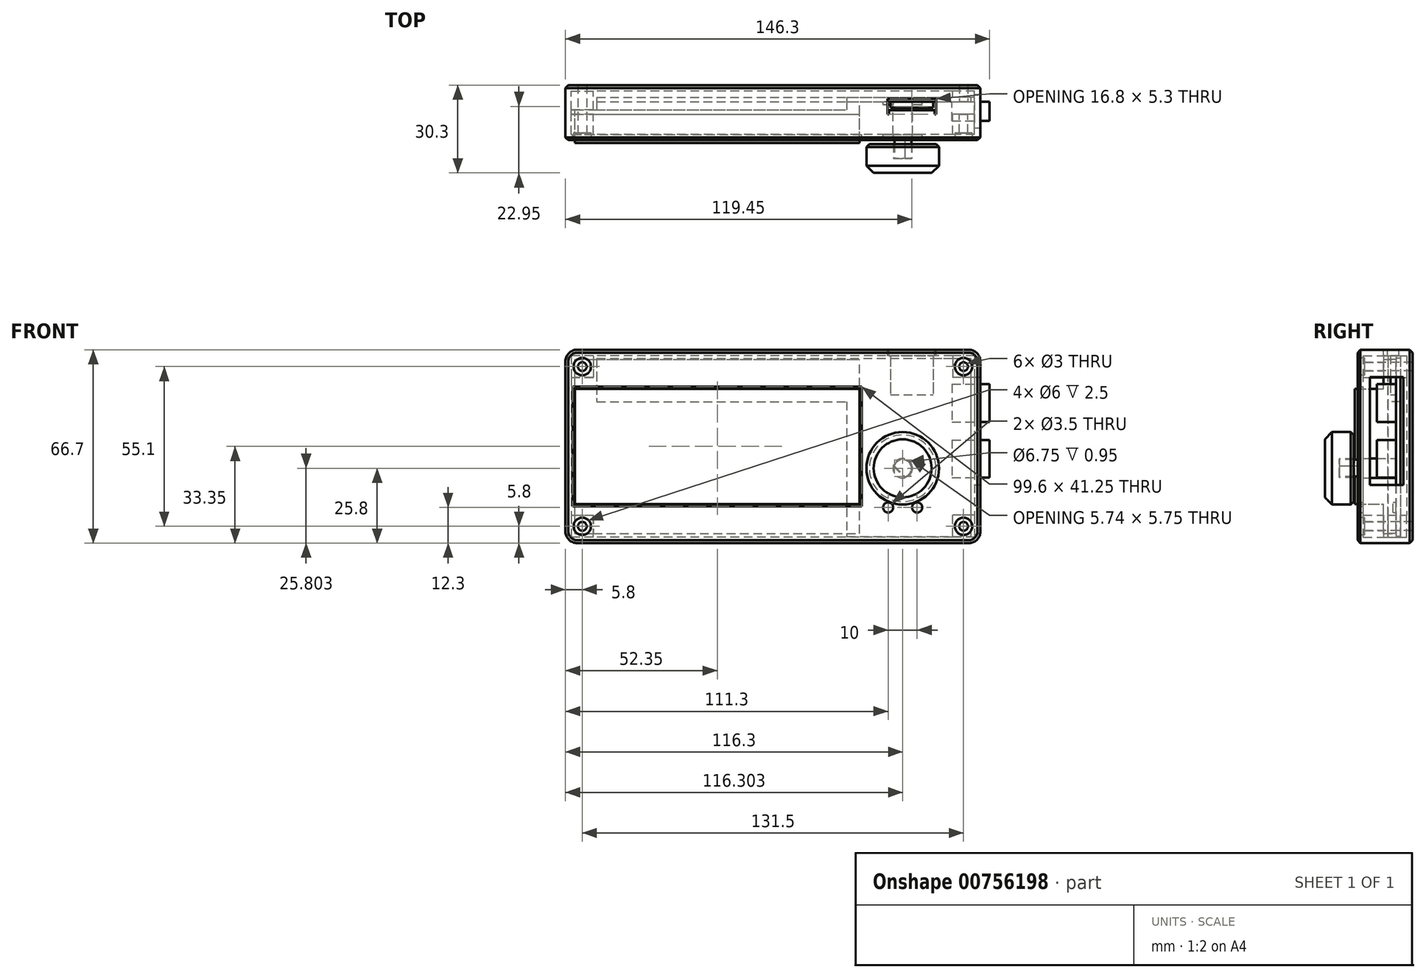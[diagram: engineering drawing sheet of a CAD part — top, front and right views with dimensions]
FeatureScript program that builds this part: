
annotation { "Feature Type Name" : "Feature", "Feature Type Description" : "" }
export const myFeature = defineFeature(function(context is Context, id is Id, definition is map)
    precondition{}
    {
        {
            var Q0;
            Q0=qCreatedBy(makeId("Front.planeOp"),FACE);
            var sketch = newSketch(context, id + "F0", { "sketchPlane" : qUnion([Q0])});
            skLineSegment(sketch, "E0.bottom", {"start": v(0, 0) * mm, "end": v(98.1, 0) * mm});
            skLineSegment(sketch, "E0.top", {"start": v(0, 60.1) * mm, "end": v(98.1, 60.1) * mm});
            skLineSegment(sketch, "E0.left", {"start": v(0, 0) * mm, "end": v(0, 60.1) * mm});
            skLineSegment(sketch, "E0.right", {"start": v(98.1, 0) * mm, "end": v(98.1, 60.1) * mm});
            skLineSegment(sketch, "E1.bottom", {"start": v(7.5, 60.5) * mm, "end": v(136.5, 60.5) * mm});
            skLineSegment(sketch, "E1.top", {"start": v(7.5, -1) * mm, "end": v(136.5, -1) * mm});
            skLineSegment(sketch, "E1.left", {"start": v(7.5, 60.5) * mm, "end": v(7.5, -1) * mm});
            skLineSegment(sketch, "E1.right", {"start": v(136.5, 60.5) * mm, "end": v(136.5, -1) * mm});
            skLineSegment(sketch, "E2", {"start": v(7.5, 45.5) * mm, "end": v(93.65, 45.5) * mm});
            skLineSegment(sketch, "E3", {"start": v(93.65, 45.5) * mm, "end": v(93.65, -1) * mm});
            skSolve(sketch);
        }
        {
            var Q0;
            {var subQ4=sQuery(id+"F0.wireOp",EDGE,"E0.left");Q0=makeQuery(id+"F0.imprint","IMPRINT",FACE,{"disambiguationData":[TD([[makeQuery(id+"F0.imprint","IMPRINT",EDGE,{"derivedFrom":subQ4}),-1.0]])]});}
            var Q1;
            {var subQ5=sQuery(id+"F0.wireOp",EDGE,"E2");Q1=makeQuery(id+"F0.imprint","IMPRINT",FACE,{"disambiguationData":[TD([[makeQuery(id+"F0.imprint","IMPRINT",EDGE,{"derivedFrom":subQ5}),-1.0]])]});}
            var Q2;
            {var subQ4=sQuery(id+"F0.wireOp",EDGE,"E0.right");Q2=makeQuery(id+"F0.imprint","IMPRINT",FACE,{"disambiguationData":[TD([[makeQuery(id+"F0.imprint","IMPRINT",EDGE,{"derivedFrom":subQ4}),1.0]])]});}
            extrude(context, id + "F1", {"entities" : qUnion([Q0, Q1, Q2]), "depth" : 1.5 * mm, "offsetDistance" : 25 * mm});
        }
        {
            var Q0;
            {var subQ0=sQuery(id+"F0.wireOp",EDGE,"E0.right");Q0=makeQuery(id+"F0.imprint","IMPRINT",FACE,{"disambiguationData":[TD([[makeQuery(id+"F0.imprint","IMPRINT",EDGE,{"derivedFrom":subQ0}),-1.0]])]});}
            var Q1;
            {var subQ4=sQuery(id+"F0.wireOp",EDGE,"E0.right");Q1=makeQuery(id+"F0.imprint","IMPRINT",FACE,{"disambiguationData":[TD([[makeQuery(id+"F0.imprint","IMPRINT",EDGE,{"derivedFrom":subQ4}),1.0]])]});}
            extrude(context, id + "F2", {"entities" : qUnion([Q0, Q1]), "operationType" : NewBodyOperationType.ADD, "oppositeDirection" : true, "depth" : (5.8 - 1.5) * mm, "offsetDistance" : 25 * mm});
        }
        {
            var Q0;
            {var subQ0=sQuery(id+"F0.wireOp",EDGE,"E0.right");Q0=makeQuery(id+"F0.imprint","IMPRINT",FACE,{"disambiguationData":[TD([[makeQuery(id+"F0.imprint","IMPRINT",EDGE,{"derivedFrom":subQ0}),-1.0]])]});}
            extrude(context, id + "F3", {"entities" : qUnion([Q0]), "operationType" : NewBodyOperationType.REMOVE, "oppositeDirection" : true, "depth" : (4.3 - 1.5) * mm, "offsetDistance" : 25 * mm});
        }
        {
            var Q0;
            Q0=makeQuery(id+"F1.opExtrude","CAP_FACE",FACE,{"disambiguationData":[OSD([sQuery(id+"F0.wireOp",EDGE,"E0.bottom"),sQuery(id+"F0.wireOp",EDGE,"E0.top"),sQuery(id+"F0.wireOp",EDGE,"E0.left"),sQuery(id+"F0.wireOp",EDGE,"E0.right")])],"isStart":false});
            var sketch = newSketch(context, id + "F4", { "sketchPlane" : qUnion([Q0])});
            skLineSegment(sketch, "E4", {"start": v(134, 75.3) * mm, "end": v(134, -5.6) * mm, "construction": true});
            skLineSegment(sketch, "E5", {"start": v(2.5, -7.78) * mm, "end": v(2.5, 68.25) * mm, "construction": true});
            skLineSegment(sketch, "E6", {"start": v(-8.17, 57.6) * mm, "end": v(158.55, 57.6) * mm, "construction": true});
            skLineSegment(sketch, "E7", {"start": v(-20.39, 2.5) * mm, "end": v(153.11, 2.5) * mm, "construction": true});
            skCircle(sketch, "E8", {"center": v(2.5, 57.6) * mm, "radius": 1.5 * mm});
            skCircle(sketch, "E9", {"center": v(2.5, 2.5) * mm, "radius": 1.5 * mm});
            skCircle(sketch, "E10", {"center": v(134, 2.5) * mm, "radius": 1.5 * mm});
            skCircle(sketch, "E11", {"center": v(134, 57.6) * mm, "radius": 1.5 * mm});
            skSolve(sketch);
        }
        {
            var Q0;
            Q0 = qSketchRegion(id + "F4", true);
            extrude(context, id + "F5", {"entities" : qUnion([Q0]), "operationType" : NewBodyOperationType.REMOVE, "oppositeDirection" : true, "depth" : 25 * mm, "offsetDistance" : 25 * mm});
        }
        {
            var Q0;
            Q0=makeQuery(id+"F1.opExtrude","CAP_FACE",FACE,{"disambiguationData":[OSD([sQuery(id+"F0.wireOp",EDGE,"E0.bottom"),sQuery(id+"F0.wireOp",EDGE,"E0.top"),sQuery(id+"F0.wireOp",EDGE,"E0.left"),sQuery(id+"F0.wireOp",EDGE,"E0.right")])],"isStart":false});
            var sketch = newSketch(context, id + "F6", { "sketchPlane" : qUnion([Q0])});
            skLineSegment(sketch, "E12.bottom", {"start": v(0, 10.18) * mm, "end": v(98.1, 10.18) * mm});
            skLineSegment(sketch, "E12.top", {"start": v(0, 49.93) * mm, "end": v(98.1, 49.93) * mm});
            skLineSegment(sketch, "E12.left", {"start": v(0, 10.18) * mm, "end": v(0, 49.93) * mm});
            skLineSegment(sketch, "E12.right", {"start": v(98.1, 10.18) * mm, "end": v(98.1, 49.93) * mm});
            skLineSegment(sketch, "E13", {"start": v(0, 30.05) * mm, "end": v(98.1, 30.05) * mm, "construction": true});
            skSolve(sketch);
        }
        {
            var Q0;
            Q0 = qSketchRegion(id + "F6", true);
            extrude(context, id + "F7", {"entities" : qUnion([Q0]), "operationType" : NewBodyOperationType.ADD, "depth" : (11.5 - 1.5) * mm, "offsetDistance" : 25 * mm});
        }
        {
            var Q0;
            Q0=makeQuery(id+"F3.boolean.opBoolean","COPY",FACE,{"derivedFrom":makeQuery(id+"F3.opExtrude","CAP_FACE",FACE,{"disambiguationData":[OSD([sQuery(id+"F0.wireOp",EDGE,"E0.bottom"),sQuery(id+"F0.wireOp",EDGE,"E0.top"),sQuery(id+"F0.wireOp",EDGE,"E0.right"),sQuery(id+"F0.wireOp",EDGE,"E1.bottom"),sQuery(id+"F0.wireOp",EDGE,"E1.top"),sQuery(id+"F0.wireOp",EDGE,"E1.left"),sQuery(id+"F0.wireOp",EDGE,"E1.right"),sQuery(id+"F0.wireOp",EDGE,"E3")])],"isStart":false})});
            var sketch = newSketch(context, id + "F8", { "sketchPlane" : qUnion([Q0])});
            skCircle(sketch, "E14", {"center": v(113, 22.5) * mm, "radius": 3.38 * mm});
            skCircle(sketch, "E15", {"center": v(108, 9) * mm, "radius": 1.75 * mm});
            skCircle(sketch, "E16", {"center": v(118, 9) * mm, "radius": 1.75 * mm});
            skSolve(sketch);
        }
        {
            var Q0;
            Q0=makeQuery(id+"F8.imprint","IMPRINT",FACE,{"disambiguationData":[TD([[makeQuery(id+"F8.imprint","IMPRINT",EDGE,{"derivedFrom":sQuery(id+"F8.wireOp",EDGE,"E14")}),1.0]])]});
            extrude(context, id + "F9", {"entities" : qUnion([Q0]), "operationType" : NewBodyOperationType.ADD, "depth" : (21.1 - 1.5) * mm, "offsetDistance" : 25 * mm});
        }
        {
            var Q0;
            Q0=makeQuery(id+"F8.imprint","IMPRINT",FACE,{"disambiguationData":[TD([[makeQuery(id+"F8.imprint","IMPRINT",EDGE,{"derivedFrom":sQuery(id+"F8.wireOp",EDGE,"E15")}),1.0]])]});
            var Q1;
            Q1=makeQuery(id+"F8.imprint","IMPRINT",FACE,{"disambiguationData":[TD([[makeQuery(id+"F8.imprint","IMPRINT",EDGE,{"derivedFrom":sQuery(id+"F8.wireOp",EDGE,"E16")}),1.0]])]});
            extrude(context, id + "F10", {"entities" : qUnion([Q0, Q1]), "operationType" : NewBodyOperationType.ADD, "depth" : 1 * mm, "offsetDistance" : 25 * mm});
        }
        {
            var Q0;
            Q0=makeQuery(id+"F8.imprint","IMPRINT",FACE,{"disambiguationData":[TD([[makeQuery(id+"F8.imprint","IMPRINT",EDGE,{"derivedFrom":sQuery(id+"F8.wireOp",EDGE,"E14")}),-1.0]])]});
            var sketch = newSketch(context, id + "F11", { "sketchPlane" : qUnion([Q0])});
            skLineSegment(sketch, "E17.bottom", {"start": v(108.75, 62.5) * mm, "end": v(123.55, 62.5) * mm});
            skLineSegment(sketch, "E17.top", {"start": v(108.75, 47.9) * mm, "end": v(123.55, 47.9) * mm});
            skLineSegment(sketch, "E17.left", {"start": v(108.75, 62.5) * mm, "end": v(108.75, 47.9) * mm});
            skLineSegment(sketch, "E17.right", {"start": v(123.55, 62.5) * mm, "end": v(123.55, 47.9) * mm});
            skSolve(sketch);
        }
        {
            var Q0;
            Q0 = qSketchRegion(id + "F11", true);
            extrude(context, id + "F12", {"entities" : qUnion([Q0]), "operationType" : NewBodyOperationType.ADD, "depth" : 2 * mm, "offsetDistance" : 25 * mm});
        }
        {
            var Q0;
            Q0=makeQuery(id+"F2.opExtrude","CAP_FACE",FACE,{"disambiguationData":[OSD([sQuery(id+"F0.wireOp",EDGE,"E1.bottom"),sQuery(id+"F0.wireOp",EDGE,"E1.top"),sQuery(id+"F0.wireOp",EDGE,"E1.left"),sQuery(id+"F0.wireOp",EDGE,"E1.right"),sQuery(id+"F0.wireOp",EDGE,"E2"),sQuery(id+"F0.wireOp",EDGE,"E3")])],"isStart":false});
            cPlane(context, id + "F13", {"entities" : qUnion([Q0]), "cplaneType" : CPlaneType.OFFSET, "offset" : (10 - 5.8) * mm, "width" : 150 * mm, "height" : 150 * mm});
        }
        {
            var Q0;
            Q0=qCreatedBy(id+"F13.planeOp",FACE);
            var sketch = newSketch(context, id + "F14", { "sketchPlane" : qUnion([Q0])});
            skLineSegment(sketch, "E18.bottom", {"start": v(-137.8, 61.4) * mm, "end": v(1.3, 61.4) * mm, "construction": true});
            skLineSegment(sketch, "E18.top", {"start": v(-137.8, -1.3) * mm, "end": v(1.3, -1.3) * mm, "construction": true});
            skLineSegment(sketch, "E18.left", {"start": v(-137.8, 61.4) * mm, "end": v(-137.8, -1.3) * mm, "construction": true});
            skLineSegment(sketch, "E18.right", {"start": v(1.3, 61.4) * mm, "end": v(1.3, -1.3) * mm, "construction": true});
            skLineSegment(sketch, "E19.0", {"start": v(-135.8, 63.4) * mm, "end": v(-0.7, 63.4) * mm});
            skLineSegment(sketch, "E19.1", {"start": v(-139.8, 59.4) * mm, "end": v(-139.8, 0.7) * mm});
            skLineSegment(sketch, "E19.2", {"start": v(-135.8, -3.3) * mm, "end": v(-0.7, -3.3) * mm});
            skLineSegment(sketch, "E19.3", {"start": v(3.3, 59.4) * mm, "end": v(3.3, 0.7) * mm});
            skPoint(sketch, "E20.visualSharp", {"position": v(3.3, 63.4) * mm});
            skArc(sketch, "E20.filletArc", {"start": v(3.3, 59.4) * mm, "mid": v(2.13, 62.23) * mm, "end": v(-0.7, 63.4) * mm});
            skPoint(sketch, "E21.visualSharp", {"position": v(-139.8, 63.4) * mm});
            skArc(sketch, "E21.filletArc", {"start": v(-135.8, 63.4) * mm, "mid": v(-138.63, 62.23) * mm, "end": v(-139.8, 59.4) * mm});
            skPoint(sketch, "E22.visualSharp", {"position": v(-139.8, -3.3) * mm});
            skArc(sketch, "E22.filletArc", {"start": v(-139.8, 0.7) * mm, "mid": v(-138.63, -2.13) * mm, "end": v(-135.8, -3.3) * mm});
            skPoint(sketch, "E23.visualSharp", {"position": v(3.3, -3.3) * mm});
            skArc(sketch, "E23.filletArc", {"start": v(-0.7, -3.3) * mm, "mid": v(2.13, -2.13) * mm, "end": v(3.3, 0.7) * mm});
            skPoint(sketch, "E24", {"position": v(-134, 57.6) * mm});
            skPoint(sketch, "E25", {"position": v(-2.5, 2.5) * mm});
            skPoint(sketch, "E26", {"position": v(-134, 2.5) * mm});
            skCircle(sketch, "E27.0", {"center": v(-134, 2.5) * mm, "radius": 1.5 * mm});
            skCircle(sketch, "E28.0", {"center": v(-134, 57.6) * mm, "radius": 1.5 * mm});
            skCircle(sketch, "E29.0", {"center": v(-2.5, 57.6) * mm, "radius": 1.5 * mm});
            skCircle(sketch, "E30.0", {"center": v(-2.5, 2.5) * mm, "radius": 1.5 * mm});
            skSolve(sketch);
        }
        {
            var Q0;
            Q0 = qSketchRegion(id + "F14", true);
            extrude(context, id + "F15", {"entities" : qUnion([Q0]), "oppositeDirection" : true, "depth" : 2 * mm, "offsetDistance" : 25 * mm});
        }
        {
            var Q0;
            Q0=makeQuery(id+"F15.opExtrude","CAP_FACE",FACE,{"disambiguationData":[OSD([sQuery(id+"F14.wireOp",EDGE,"E19.0"),sQuery(id+"F14.wireOp",EDGE,"E19.1"),sQuery(id+"F14.wireOp",EDGE,"E19.2"),sQuery(id+"F14.wireOp",EDGE,"E19.3"),sQuery(id+"F14.wireOp",EDGE,"E20.filletArc"),sQuery(id+"F14.wireOp",EDGE,"E21.filletArc"),sQuery(id+"F14.wireOp",EDGE,"E22.filletArc"),sQuery(id+"F14.wireOp",EDGE,"E23.filletArc"),sQuery(id+"F14.wireOp",EDGE,"E27.0"),sQuery(id+"F14.wireOp",EDGE,"E28.0"),sQuery(id+"F14.wireOp",EDGE,"E29.0"),sQuery(id+"F14.wireOp",EDGE,"E30.0")])],"isStart":false});
            var sketch = newSketch(context, id + "F16", { "sketchPlane" : qUnion([Q0])});
            skLineSegment(sketch, "E31.0", {"start": v(139.8, 59.4) * mm, "end": v(139.8, 0.7) * mm});
            skArc(sketch, "E31.1", {"start": v(135.8, 63.4) * mm, "mid": v(138.63, 62.23) * mm, "end": v(139.8, 59.4) * mm});
            skLineSegment(sketch, "E31.2", {"start": v(135.8, 63.4) * mm, "end": v(0.7, 63.4) * mm});
            skArc(sketch, "E31.3", {"start": v(-3.3, 59.4) * mm, "mid": v(-2.13, 62.23) * mm, "end": v(0.7, 63.4) * mm});
            skLineSegment(sketch, "E31.4", {"start": v(-3.3, 59.4) * mm, "end": v(-3.3, 0.7) * mm});
            skArc(sketch, "E31.5", {"start": v(0.7, -3.3) * mm, "mid": v(-2.13, -2.13) * mm, "end": v(-3.3, 0.7) * mm});
            skLineSegment(sketch, "E31.6", {"start": v(135.8, -3.3) * mm, "end": v(0.7, -3.3) * mm});
            skArc(sketch, "E31.7", {"start": v(139.8, 0.7) * mm, "mid": v(138.63, -2.13) * mm, "end": v(135.8, -3.3) * mm});
            skLineSegment(sketch, "E32.0", {"start": v(-1.3, 61.4) * mm, "end": v(-1.3, -1.3) * mm});
            skLineSegment(sketch, "E32.1", {"start": v(137.8, 61.4) * mm, "end": v(-1.3, 61.4) * mm});
            skLineSegment(sketch, "E32.2", {"start": v(137.8, 61.4) * mm, "end": v(137.8, -1.3) * mm});
            skLineSegment(sketch, "E32.3", {"start": v(137.8, -1.3) * mm, "end": v(-1.3, -1.3) * mm});
            skSolve(sketch);
        }
        {
            var Q0;
            Q0 = qSketchRegion(id + "F16", true);
            extrude(context, id + "F17", {"entities" : qUnion([Q0]), "operationType" : NewBodyOperationType.ADD, "depth" : 8 * mm, "offsetDistance" : 25 * mm});
        }
        {
            var Q0;
            Q0=makeQuery(id+"F15.opExtrude","CAP_FACE",FACE,{"disambiguationData":[OSD([sQuery(id+"F14.wireOp",EDGE,"E19.0"),sQuery(id+"F14.wireOp",EDGE,"E19.1"),sQuery(id+"F14.wireOp",EDGE,"E19.2"),sQuery(id+"F14.wireOp",EDGE,"E19.3"),sQuery(id+"F14.wireOp",EDGE,"E20.filletArc"),sQuery(id+"F14.wireOp",EDGE,"E21.filletArc"),sQuery(id+"F14.wireOp",EDGE,"E22.filletArc"),sQuery(id+"F14.wireOp",EDGE,"E23.filletArc"),sQuery(id+"F14.wireOp",EDGE,"E27.0"),sQuery(id+"F14.wireOp",EDGE,"E28.0"),sQuery(id+"F14.wireOp",EDGE,"E29.0"),sQuery(id+"F14.wireOp",EDGE,"E30.0")])],"isStart":false});
            var sketch = newSketch(context, id + "F18", { "sketchPlane" : qUnion([Q0])});
            skLineSegment(sketch, "E33.bottom", {"start": v(-1.3, 61.4) * mm, "end": v(6.3, 61.4) * mm});
            skLineSegment(sketch, "E33.top", {"start": v(-1.3, 53.8) * mm, "end": v(6.3, 53.8) * mm});
            skLineSegment(sketch, "E33.left", {"start": v(-1.3, 61.4) * mm, "end": v(-1.3, 53.8) * mm});
            skLineSegment(sketch, "E33.right", {"start": v(6.3, 61.4) * mm, "end": v(6.3, 53.8) * mm});
            skLineSegment(sketch, "E34.top", {"start": v(-1.3, 6.3) * mm, "end": v(6.3, 6.3) * mm});
            skLineSegment(sketch, "E34.left", {"start": v(-1.3, -1.3) * mm, "end": v(-1.3, 6.3) * mm});
            skLineSegment(sketch, "E34.right", {"start": v(6.3, -1.3) * mm, "end": v(6.3, 6.3) * mm});
            skLineSegment(sketch, "E35.bottom", {"start": v(137.8, -1.3) * mm, "end": v(130.2, -1.3) * mm});
            skLineSegment(sketch, "E35.top", {"start": v(137.8, 6.3) * mm, "end": v(130.2, 6.3) * mm});
            skLineSegment(sketch, "E35.left", {"start": v(137.8, -1.3) * mm, "end": v(137.8, 6.3) * mm});
            skLineSegment(sketch, "E35.right", {"start": v(130.2, -1.3) * mm, "end": v(130.2, 6.3) * mm});
            skLineSegment(sketch, "E36.bottom", {"start": v(137.8, 61.4) * mm, "end": v(130.2, 61.4) * mm});
            skLineSegment(sketch, "E36.top", {"start": v(137.8, 53.8) * mm, "end": v(130.2, 53.8) * mm});
            skLineSegment(sketch, "E36.left", {"start": v(137.8, 61.4) * mm, "end": v(137.8, 53.8) * mm});
            skLineSegment(sketch, "E36.right", {"start": v(130.2, 61.4) * mm, "end": v(130.2, 53.8) * mm});
            skSolve(sketch);
        }
        {
            var Q0;
            Q0=makeQuery(id+"F18.imprint","IMPRINT",FACE,{"disambiguationData":[TD([[makeQuery(id+"F18.imprint","IMPRINT",EDGE,{"derivedFrom":sQuery(id+"F18.wireOp",EDGE,"E33.bottom")}),1.0]])]});
            var Q1;
            Q1=makeQuery(id+"F18.imprint","IMPRINT",FACE,{"disambiguationData":[TD([[makeQuery(id+"F18.imprint","IMPRINT",EDGE,{"derivedFrom":sQuery(id+"F18.wireOp",EDGE,"E34.top")}),-1.0]])]});
            extrude(context, id + "F19", {"entities" : qUnion([Q0, Q1]), "operationType" : NewBodyOperationType.ADD, "depth" : 6.5 * mm, "offsetDistance" : 25 * mm});
        }
        {
            var Q0;
            Q0=makeQuery(id+"F18.imprint","IMPRINT",FACE,{"disambiguationData":[TD([[makeQuery(id+"F18.imprint","IMPRINT",EDGE,{"derivedFrom":sQuery(id+"F18.wireOp",EDGE,"E36.bottom")}),1.0]])]});
            var Q1;
            Q1=makeQuery(id+"F18.imprint","IMPRINT",FACE,{"disambiguationData":[TD([[makeQuery(id+"F18.imprint","IMPRINT",EDGE,{"derivedFrom":sQuery(id+"F18.wireOp",EDGE,"E35.bottom")}),-1.0]])]});
            extrude(context, id + "F20", {"entities" : qUnion([Q0, Q1]), "operationType" : NewBodyOperationType.ADD, "depth" : 2.2 * mm, "offsetDistance" : 25 * mm});
        }
        {
            var Q0;
            Q0=makeQuery(id+"F17.opExtrude","CAP_FACE",FACE,{"disambiguationData":[OSD([sQuery(id+"F16.wireOp",EDGE,"E31.0"),sQuery(id+"F16.wireOp",EDGE,"E31.1"),sQuery(id+"F16.wireOp",EDGE,"E31.2"),sQuery(id+"F16.wireOp",EDGE,"E31.3"),sQuery(id+"F16.wireOp",EDGE,"E31.4"),sQuery(id+"F16.wireOp",EDGE,"E31.5"),sQuery(id+"F16.wireOp",EDGE,"E31.6"),sQuery(id+"F16.wireOp",EDGE,"E31.7"),sQuery(id+"F16.wireOp",EDGE,"E32.0"),sQuery(id+"F16.wireOp",EDGE,"E32.1"),sQuery(id+"F16.wireOp",EDGE,"E32.2"),sQuery(id+"F16.wireOp",EDGE,"E32.3")])],"isStart":false});
            var sketch = newSketch(context, id + "F21", { "sketchPlane" : qUnion([Q0])});
            skLineSegment(sketch, "E37.bottom", {"start": v(107.75, 61.4) * mm, "end": v(124.55, 61.4) * mm});
            skLineSegment(sketch, "E37.top", {"start": v(107.75, 63.4) * mm, "end": v(124.55, 63.4) * mm});
            skLineSegment(sketch, "E37.left", {"start": v(107.75, 61.4) * mm, "end": v(107.75, 63.4) * mm});
            skLineSegment(sketch, "E37.right", {"start": v(124.55, 61.4) * mm, "end": v(124.55, 63.4) * mm});
            skSolve(sketch);
        }
        {
            var Q0;
            Q0 = qSketchRegion(id + "F21", true);
            extrude(context, id + "F22", {"entities" : qUnion([Q0]), "operationType" : NewBodyOperationType.REMOVE, "oppositeDirection" : true, "depth" : 5.3 * mm, "offsetDistance" : 25 * mm});
        }
        {
            var Q0;
            Q0=makeQuery(id+"F3.boolean.opBoolean","COPY",FACE,{"derivedFrom":makeQuery(id+"F3.opExtrude","CAP_FACE",FACE,{"disambiguationData":[OSD([sQuery(id+"F0.wireOp",EDGE,"E0.bottom"),sQuery(id+"F0.wireOp",EDGE,"E0.top"),sQuery(id+"F0.wireOp",EDGE,"E0.right"),sQuery(id+"F0.wireOp",EDGE,"E1.bottom"),sQuery(id+"F0.wireOp",EDGE,"E1.top"),sQuery(id+"F0.wireOp",EDGE,"E1.left"),sQuery(id+"F0.wireOp",EDGE,"E1.right"),sQuery(id+"F0.wireOp",EDGE,"E3")])],"isStart":false})});
            var sketch = newSketch(context, id + "F23", { "sketchPlane" : qUnion([Q0])});
            skLineSegment(sketch, "E38.bottom", {"start": v(130, 51.5) * mm, "end": v(143, 51.5) * mm});
            skLineSegment(sketch, "E38.top", {"start": v(130, 38.5) * mm, "end": v(143, 38.5) * mm});
            skLineSegment(sketch, "E38.left", {"start": v(130, 51.5) * mm, "end": v(130, 38.5) * mm});
            skLineSegment(sketch, "E38.right", {"start": v(143, 51.5) * mm, "end": v(143, 38.5) * mm});
            skLineSegment(sketch, "E39.bottom", {"start": v(130, 32.3) * mm, "end": v(143, 32.3) * mm});
            skLineSegment(sketch, "E39.top", {"start": v(130, 19.3) * mm, "end": v(143, 19.3) * mm});
            skLineSegment(sketch, "E39.left", {"start": v(130, 32.3) * mm, "end": v(130, 19.3) * mm});
            skLineSegment(sketch, "E39.right", {"start": v(143, 32.3) * mm, "end": v(143, 19.3) * mm});
            skSolve(sketch);
        }
        {
            var Q0;
            Q0 = qSketchRegion(id + "F23", true);
            extrude(context, id + "F24", {"entities" : qUnion([Q0]), "operationType" : NewBodyOperationType.ADD, "depth" : 6.6 * mm, "offsetDistance" : 25 * mm});
        }
        {
            var Q0;
            Q0=makeQuery(id+"F17.boolean.opBoolean","MERGE",FACE,{"derivedFrom":[makeQuery(id+"F15.opExtrude","SWEPT_FACE",FACE,{"disambiguationData":[OSD([sQuery(id+"F14.wireOp",EDGE,"E19.1")])]}),makeQuery(id+"F17.opExtrude","SWEPT_FACE",FACE,{"disambiguationData":[OSD([sQuery(id+"F16.wireOp",EDGE,"E31.0")])]})]});
            var sketch = newSketch(context, id + "F25", { "sketchPlane" : qUnion([Q0])});
            skLineSegment(sketch, "E40.bottom", {"start": v(-1.5, 54) * mm, "end": v(5.3, 54) * mm});
            skLineSegment(sketch, "E40.top", {"start": v(-1.5, 16.8) * mm, "end": v(5.3, 16.8) * mm});
            skLineSegment(sketch, "E40.left", {"start": v(-1.5, 54) * mm, "end": v(-1.5, 16.8) * mm});
            skLineSegment(sketch, "E40.right", {"start": v(5.3, 54) * mm, "end": v(5.3, 16.8) * mm});
            skSolve(sketch);
        }
        {
            var Q0;
            Q0 = qSketchRegion(id + "F25", true);
            extrude(context, id + "F26", {"entities" : qUnion([Q0]), "operationType" : NewBodyOperationType.REMOVE, "oppositeDirection" : true, "depth" : 2 * mm, "offsetDistance" : 25 * mm});
        }
        {
            var Q0;
            Q0=makeQuery(id+"F15.opExtrude","CAP_EDGE",EDGE,{"disambiguationData":[OSD([sQuery(id+"F14.wireOp",EDGE,"E19.0")])],"isStart":true});
            var Q1;
            Q1=makeQuery(id+"F15.opExtrude","CAP_EDGE",EDGE,{"disambiguationData":[OSD([sQuery(id+"F14.wireOp",EDGE,"E21.filletArc")])],"isStart":true});
            chamfer(context, id + "F27", {"entities" : qUnion([Q0, Q1]), "width" : 1 * mm, "tangentPropagation" : true});
        }
        {
            var Q0;
            {var subQ0=sQuery(id+"F16.wireOp",EDGE,"E31.0");var subQ1=sQuery(id+"F16.wireOp",EDGE,"E31.3");var subQ2=sQuery(id+"F16.wireOp",EDGE,"E31.2");var subQ3=sQuery(id+"F16.wireOp",EDGE,"E31.4");var subQ4=sQuery(id+"F16.wireOp",EDGE,"E31.5");var subQ5=sQuery(id+"F16.wireOp",EDGE,"E31.6");var subQ6=sQuery(id+"F16.wireOp",EDGE,"E31.7");var subQ7=sQuery(id+"F16.wireOp",EDGE,"E32.0");var subQ8=sQuery(id+"F16.wireOp",EDGE,"E32.1");var subQ9=sQuery(id+"F16.wireOp",EDGE,"E32.2");var subQ10=sQuery(id+"F16.wireOp",EDGE,"E32.3");Q0=makeQuery(id+"F26.boolean.opBoolean","SPLIT",FACE,{"disambiguationData":[TD([makeQuery(id+"F15.opExtrude","SWEPT_FACE",FACE,{"disambiguationData":[OSD([sQuery(id+"F14.wireOp",EDGE,"E19.2")])]})])],"derivedFrom":makeQuery(id+"F17.opExtrude","CAP_FACE",FACE,{"disambiguationData":[OSD([subQ0,sQuery(id+"F16.wireOp",EDGE,"E31.1"),subQ2,subQ1,subQ3,subQ4,subQ5,subQ6,subQ7,subQ8,subQ9,subQ10])],"isStart":false})});}
            var sketch = newSketch(context, id + "F28", { "sketchPlane" : qUnion([Q0])});
            skLineSegment(sketch, "E41.0.0", {"start": v(137.8, 6.3) * mm, "end": v(137.8, 53.8) * mm});
            skLineSegment(sketch, "E41.0.1", {"start": v(137.8, 53.8) * mm, "end": v(130.2, 53.8) * mm});
            skLineSegment(sketch, "E41.0.2", {"start": v(130.2, 53.8) * mm, "end": v(130.2, 61.4) * mm});
            skLineSegment(sketch, "E41.0.3", {"start": v(130.2, 61.4) * mm, "end": v(6.3, 61.4) * mm});
            skLineSegment(sketch, "E41.0.4", {"start": v(6.3, 61.4) * mm, "end": v(6.3, 53.8) * mm});
            skLineSegment(sketch, "E41.0.5", {"start": v(6.3, 53.8) * mm, "end": v(-1.3, 53.8) * mm});
            skLineSegment(sketch, "E41.0.6", {"start": v(-1.3, 53.8) * mm, "end": v(-1.3, 6.3) * mm});
            skLineSegment(sketch, "E41.0.7", {"start": v(-1.3, 6.3) * mm, "end": v(6.3, 6.3) * mm});
            skLineSegment(sketch, "E41.0.8", {"start": v(6.3, 6.3) * mm, "end": v(6.3, -1.3) * mm});
            skLineSegment(sketch, "E41.0.9", {"start": v(6.3, -1.3) * mm, "end": v(130.2, -1.3) * mm});
            skLineSegment(sketch, "E41.0.10", {"start": v(130.2, -1.3) * mm, "end": v(130.2, 6.3) * mm});
            skLineSegment(sketch, "E41.0.11", {"start": v(130.2, 6.3) * mm, "end": v(137.8, 6.3) * mm});
            skLineSegment(sketch, "E42.0", {"start": v(-3.3, 59.4) * mm, "end": v(-3.3, 0.7) * mm});
            skArc(sketch, "E42.1", {"start": v(0.7, -3.3) * mm, "mid": v(-2.13, -2.13) * mm, "end": v(-3.3, 0.7) * mm});
            skLineSegment(sketch, "E42.2", {"start": v(135.8, -3.3) * mm, "end": v(0.7, -3.3) * mm});
            skArc(sketch, "E42.3", {"start": v(139.8, 0.7) * mm, "mid": v(138.63, -2.13) * mm, "end": v(135.8, -3.3) * mm});
            skLineSegment(sketch, "E42.4", {"start": v(139.8, 16.8) * mm, "end": v(139.8, 0.7) * mm});
            skLineSegment(sketch, "E42.5", {"start": v(139.8, 59.4) * mm, "end": v(139.8, 54) * mm});
            skLineSegment(sketch, "E42.6", {"start": v(139.8, 54) * mm, "end": v(139.8, 16.8) * mm});
            skArc(sketch, "E42.7", {"start": v(135.8, 63.4) * mm, "mid": v(138.63, 62.23) * mm, "end": v(139.8, 59.4) * mm});
            skLineSegment(sketch, "E42.8", {"start": v(135.8, 63.4) * mm, "end": v(124.55, 63.4) * mm});
            skLineSegment(sketch, "E42.9", {"start": v(124.55, 63.4) * mm, "end": v(107.75, 63.4) * mm});
            skLineSegment(sketch, "E42.10", {"start": v(107.75, 63.4) * mm, "end": v(0.7, 63.4) * mm});
            skArc(sketch, "E42.11", {"start": v(-3.3, 59.4) * mm, "mid": v(-2.13, 62.23) * mm, "end": v(0.7, 63.4) * mm});
            skCircle(sketch, "E42.12", {"center": v(2.5, 57.6) * mm, "radius": 1.5 * mm});
            skCircle(sketch, "E42.13", {"center": v(2.5, 2.5) * mm, "radius": 1.5 * mm});
            skCircle(sketch, "E42.14", {"center": v(134, 2.5) * mm, "radius": 1.5 * mm});
            skCircle(sketch, "E42.15", {"center": v(134, 57.6) * mm, "radius": 1.5 * mm});
            skSolve(sketch);
        }
        {
            var Q0;
            Q0 = qSketchRegion(id + "F28", true);
            extrude(context, id + "F29", {"entities" : qUnion([Q0]), "depth" : 7 * mm, "offsetDistance" : 25 * mm});
        }
        {
            var Q0;
            Q0=makeQuery(id+"F29.opExtrude","CAP_FACE",FACE,{"disambiguationData":[OSD([sQuery(id+"F28.wireOp",EDGE,"E41.0.0"),sQuery(id+"F28.wireOp",EDGE,"E41.0.1"),sQuery(id+"F28.wireOp",EDGE,"E41.0.2"),sQuery(id+"F28.wireOp",EDGE,"E41.0.3"),sQuery(id+"F28.wireOp",EDGE,"E41.0.4"),sQuery(id+"F28.wireOp",EDGE,"E41.0.5"),sQuery(id+"F28.wireOp",EDGE,"E41.0.6"),sQuery(id+"F28.wireOp",EDGE,"E41.0.7"),sQuery(id+"F28.wireOp",EDGE,"E41.0.8"),sQuery(id+"F28.wireOp",EDGE,"E41.0.9"),sQuery(id+"F28.wireOp",EDGE,"E41.0.10"),sQuery(id+"F28.wireOp",EDGE,"E41.0.11"),sQuery(id+"F28.wireOp",EDGE,"E42.0"),sQuery(id+"F28.wireOp",EDGE,"E42.1"),sQuery(id+"F28.wireOp",EDGE,"E42.2"),sQuery(id+"F28.wireOp",EDGE,"E42.3"),sQuery(id+"F28.wireOp",EDGE,"E42.4"),sQuery(id+"F28.wireOp",EDGE,"E42.5"),sQuery(id+"F28.wireOp",EDGE,"E42.6"),sQuery(id+"F28.wireOp",EDGE,"E42.7"),sQuery(id+"F28.wireOp",EDGE,"E42.8"),sQuery(id+"F28.wireOp",EDGE,"E42.9"),sQuery(id+"F28.wireOp",EDGE,"E42.10"),sQuery(id+"F28.wireOp",EDGE,"E42.11"),sQuery(id+"F28.wireOp",EDGE,"E42.12"),sQuery(id+"F28.wireOp",EDGE,"E42.13"),sQuery(id+"F28.wireOp",EDGE,"E42.14"),sQuery(id+"F28.wireOp",EDGE,"E42.15")])],"isStart":false});
            var sketch = newSketch(context, id + "F30", { "sketchPlane" : qUnion([Q0])});
            skLineSegment(sketch, "E43.0", {"start": v(-3.3, 59.4) * mm, "end": v(-3.3, 0.7) * mm});
            skArc(sketch, "E43.1", {"start": v(0.7, -3.3) * mm, "mid": v(-2.13, -2.13) * mm, "end": v(-3.3, 0.7) * mm});
            skLineSegment(sketch, "E43.2", {"start": v(135.8, -3.3) * mm, "end": v(0.7, -3.3) * mm});
            skArc(sketch, "E43.3", {"start": v(139.8, 0.7) * mm, "mid": v(138.63, -2.13) * mm, "end": v(135.8, -3.3) * mm});
            skLineSegment(sketch, "E43.4", {"start": v(139.8, 59.4) * mm, "end": v(139.8, 0.7) * mm});
            skArc(sketch, "E43.5", {"start": v(135.8, 63.4) * mm, "mid": v(138.63, 62.23) * mm, "end": v(139.8, 59.4) * mm});
            skLineSegment(sketch, "E43.6", {"start": v(135.8, 63.4) * mm, "end": v(0.7, 63.4) * mm});
            skArc(sketch, "E43.7", {"start": v(-3.3, 59.4) * mm, "mid": v(-2.13, 62.23) * mm, "end": v(0.7, 63.4) * mm});
            skCircle(sketch, "E43.8", {"center": v(2.5, 57.6) * mm, "radius": 1.5 * mm});
            skCircle(sketch, "E43.9", {"center": v(2.5, 2.5) * mm, "radius": 1.5 * mm});
            skCircle(sketch, "E43.10", {"center": v(134, 2.5) * mm, "radius": 1.5 * mm});
            skCircle(sketch, "E43.11", {"center": v(134, 57.6) * mm, "radius": 1.5 * mm});
            skLineSegment(sketch, "E44.0", {"start": v(-0.75, 50.68) * mm, "end": v(98.85, 50.68) * mm});
            skLineSegment(sketch, "E44.1", {"start": v(-0.75, 9.43) * mm, "end": v(-0.75, 50.68) * mm});
            skLineSegment(sketch, "E44.2", {"start": v(-0.75, 9.43) * mm, "end": v(98.85, 9.43) * mm});
            skLineSegment(sketch, "E44.3", {"start": v(98.85, 9.43) * mm, "end": v(98.85, 50.68) * mm});
            skCircle(sketch, "E45.0", {"center": v(108, 9) * mm, "radius": 1.75 * mm});
            skCircle(sketch, "E46.0", {"center": v(118, 9) * mm, "radius": 1.75 * mm});
            skCircle(sketch, "E47.0", {"center": v(113, 22.5) * mm, "radius": 3.38 * mm});
            skSolve(sketch);
        }
        {
            var Q0;
            Q0 = qSketchRegion(id + "F30", true);
            extrude(context, id + "F31", {"entities" : qUnion([Q0]), "operationType" : NewBodyOperationType.ADD, "depth" : 2 * mm, "offsetDistance" : 25 * mm});
        }
        {
            var Q0;
            Q0=makeQuery(id+"F31.opExtrude","CAP_FACE",FACE,{"disambiguationData":[OSD([sQuery(id+"F30.wireOp",EDGE,"E43.0"),sQuery(id+"F30.wireOp",EDGE,"E43.1"),sQuery(id+"F30.wireOp",EDGE,"E43.2"),sQuery(id+"F30.wireOp",EDGE,"E43.3"),sQuery(id+"F30.wireOp",EDGE,"E43.4"),sQuery(id+"F30.wireOp",EDGE,"E43.5"),sQuery(id+"F30.wireOp",EDGE,"E43.6"),sQuery(id+"F30.wireOp",EDGE,"E43.7"),sQuery(id+"F30.wireOp",EDGE,"E43.8"),sQuery(id+"F30.wireOp",EDGE,"E43.9"),sQuery(id+"F30.wireOp",EDGE,"E43.10"),sQuery(id+"F30.wireOp",EDGE,"E43.11"),sQuery(id+"F30.wireOp",EDGE,"E44.0"),sQuery(id+"F30.wireOp",EDGE,"E44.1"),sQuery(id+"F30.wireOp",EDGE,"E44.2"),sQuery(id+"F30.wireOp",EDGE,"E44.3"),sQuery(id+"F30.wireOp",EDGE,"E45.0"),sQuery(id+"F30.wireOp",EDGE,"E46.0"),sQuery(id+"F30.wireOp",EDGE,"E47.0")])],"isStart":false});
            var sketch = newSketch(context, id + "F32", { "sketchPlane" : qUnion([Q0])});
            skCircle(sketch, "E48", {"center": v(2.5, 57.6) * mm, "radius": 3 * mm});
            skCircle(sketch, "E49", {"center": v(2.5, 2.5) * mm, "radius": 3 * mm});
            skCircle(sketch, "E50", {"center": v(134, 2.5) * mm, "radius": 3 * mm});
            skCircle(sketch, "E51", {"center": v(134, 57.6) * mm, "radius": 3 * mm});
            skSolve(sketch);
        }
        {
            var Q0;
            Q0 = qSketchRegion(id + "F32", true);
            extrude(context, id + "F33", {"entities" : qUnion([Q0]), "operationType" : NewBodyOperationType.REMOVE, "oppositeDirection" : true, "depth" : 2.5 * mm, "offsetDistance" : 25 * mm});
        }
        {
            var Q0;
            Q0=makeQuery(id+"F31.boolean.opBoolean","MERGE",FACE,{"derivedFrom":[makeQuery(id+"F29.opExtrude","SWEPT_FACE",FACE,{"disambiguationData":[OSD([sQuery(id+"F28.wireOp",EDGE,"E42.4"),sQuery(id+"F28.wireOp",EDGE,"E42.5"),sQuery(id+"F28.wireOp",EDGE,"E42.6")])]}),makeQuery(id+"F31.opExtrude","SWEPT_FACE",FACE,{"disambiguationData":[OSD([sQuery(id+"F30.wireOp",EDGE,"E43.4")])]})]});
            var sketch = newSketch(context, id + "F34", { "sketchPlane" : qUnion([Q0])});
            skLineSegment(sketch, "E52.bottom", {"start": v(-1.5, 54) * mm, "end": v(-6.3, 54) * mm});
            skLineSegment(sketch, "E52.top", {"start": v(-1.5, 16.8) * mm, "end": v(-6.3, 16.8) * mm});
            skLineSegment(sketch, "E52.left", {"start": v(-1.5, 54) * mm, "end": v(-1.5, 16.8) * mm});
            skLineSegment(sketch, "E52.right", {"start": v(-6.3, 54) * mm, "end": v(-6.3, 16.8) * mm});
            skSolve(sketch);
        }
        {
            var Q0;
            Q0 = qSketchRegion(id + "F34", true);
            extrude(context, id + "F35", {"entities" : qUnion([Q0]), "operationType" : NewBodyOperationType.REMOVE, "oppositeDirection" : true, "depth" : 2 * mm, "offsetDistance" : 25 * mm});
        }
        {
            var Q0;
            Q0=makeQuery(id+"F31.boolean.opBoolean","MERGE",FACE,{"derivedFrom":[makeQuery(id+"F29.opExtrude","SWEPT_FACE",FACE,{"disambiguationData":[OSD([sQuery(id+"F28.wireOp",EDGE,"E42.8"),sQuery(id+"F28.wireOp",EDGE,"E42.9"),sQuery(id+"F28.wireOp",EDGE,"E42.10")])]}),makeQuery(id+"F31.opExtrude","SWEPT_FACE",FACE,{"disambiguationData":[OSD([sQuery(id+"F30.wireOp",EDGE,"E43.6")])]})]});
            var sketch = newSketch(context, id + "F36", { "sketchPlane" : qUnion([Q0])});
            skLineSegment(sketch, "E53.bottom", {"start": v(108.25, -1.5) * mm, "end": v(124.05, -1.5) * mm});
            skLineSegment(sketch, "E53.top", {"start": v(108.25, -0.2) * mm, "end": v(124.05, -0.2) * mm});
            skLineSegment(sketch, "E53.left", {"start": v(108.25, -1.5) * mm, "end": v(108.25, -0.2) * mm});
            skLineSegment(sketch, "E53.right", {"start": v(124.05, -1.5) * mm, "end": v(124.05, -0.2) * mm});
            skSolve(sketch);
        }
        {
            var Q0;
            Q0 = qSketchRegion(id + "F36", true);
            extrude(context, id + "F37", {"entities" : qUnion([Q0]), "operationType" : NewBodyOperationType.ADD, "oppositeDirection" : true, "depth" : 2 * mm, "offsetDistance" : 25 * mm});
        }
        {
            var Q0;
            Q0=makeQuery(id+"F31.opExtrude","CAP_EDGE",EDGE,{"disambiguationData":[OSD([sQuery(id+"F30.wireOp",EDGE,"E43.6")])],"isStart":false});
            chamfer(context, id + "F38", {"entities" : qUnion([Q0]), "width" : 1 * mm, "tangentPropagation" : true});
        }
        {
            var Q0;
            Q0=makeQuery(id+"F9.opExtrude","CAP_FACE",FACE,{"disambiguationData":[OSD([sQuery(id+"F8.wireOp",EDGE,"E14")])],"isStart":false});
            var sketch = newSketch(context, id + "F39", { "sketchPlane" : qUnion([Q0])});
            skCircle(sketch, "E54", {"center": v(113, 22.5) * mm, "radius": 2.98 * mm});
            skLineSegment(sketch, "E55", {"start": v(110.13, 23.3) * mm, "end": v(113.78, 19.63) * mm});
            skCircle(sketch, "E56.0", {"center": v(113, 22.5) * mm, "radius": 3.38 * mm});
            skSolve(sketch);
        }
        {
            var Q0;
            Q0 = qSketchRegion(id + "F39", true);
            var Q1;
            {var subQ0=sQuery(id+"F39.wireOp",EDGE,"E55");Q1=makeQuery(id+"F39.imprint","IMPRINT",FACE,{"disambiguationData":[TD([[makeQuery(id+"F39.imprint","IMPRINT",EDGE,{"derivedFrom":subQ0}),-1.0]])]});}
            extrude(context, id + "F40", {"entities" : qUnion([Q0, Q1]), "operationType" : NewBodyOperationType.REMOVE, "oppositeDirection" : true, "depth" : 7.25 * mm, "offsetDistance" : 25 * mm});
        }
        {
            var Q0;
            Q0=makeQuery(id+"F9.opExtrude","CAP_FACE",FACE,{"disambiguationData":[OSD([sQuery(id+"F8.wireOp",EDGE,"E14")])],"isStart":false});
            var sketch = newSketch(context, id + "F41", { "sketchPlane" : qUnion([Q0])});
            skCircle(sketch, "E57", {"center": v(113, 22.5) * mm, "radius": 12.5 * mm});
            skArc(sketch, "E58.0", {"start": v(113.7, 19.35) * mm, "mid": v(115.29, 24.78) * mm, "end": v(109.86, 23.21) * mm});
            skLineSegment(sketch, "E58.1", {"start": v(109.86, 23.21) * mm, "end": v(113.7, 19.35) * mm});
            skSolve(sketch);
        }
        {
            var Q0;
            Q0 = qSketchRegion(id + "F41", true);
            extrude(context, id + "F42", {"entities" : qUnion([Q0]), "oppositeDirection" : true, "depth" : 5 * mm, "offsetDistance" : 25 * mm});
        }
        {
            var Q0;
            Q0=makeQuery(id+"F42.opExtrude","CAP_FACE",FACE,{"disambiguationData":[OSD([sQuery(id+"F41.wireOp",EDGE,"E57"),sQuery(id+"F41.wireOp",EDGE,"wC6XnDKo-mN2I-A4Jm-05fF-ht4Pu2aToeow")])],"isStart":true});
            var sketch = newSketch(context, id + "F43", { "sketchPlane" : qUnion([Q0])});
            skCircle(sketch, "E59.0", {"center": v(113, 22.5) * mm, "radius": 12.5 * mm});
            skSolve(sketch);
        }
        {
            var Q0;
            Q0 = qSketchRegion(id + "F43", true);
            extrude(context, id + "F44", {"entities" : qUnion([Q0]), "operationType" : NewBodyOperationType.ADD, "depth" : 5 * mm, "offsetDistance" : 25 * mm});
        }
        {
            var Q0;
            Q0=makeQuery(id+"F44.opExtrude","CAP_EDGE",EDGE,{"disambiguationData":[OSD([sQuery(id+"F43.wireOp",EDGE,"E59.0")])],"isStart":false});
            chamfer(context, id + "F45", {"entities" : qUnion([Q0]), "width" : 2.5 * mm, "tangentPropagation" : true});
        }
        {
            var Q0;
            Q0=makeQuery(id+"F42.opExtrude","CAP_EDGE",EDGE,{"disambiguationData":[OSD([sQuery(id+"F41.wireOp",EDGE,"E57")])],"isStart":false});
            chamfer(context, id + "F46", {"entities" : qUnion([Q0]), "width" : 1 * mm, "tangentPropagation" : true});
        }
    });
